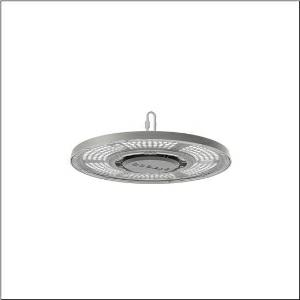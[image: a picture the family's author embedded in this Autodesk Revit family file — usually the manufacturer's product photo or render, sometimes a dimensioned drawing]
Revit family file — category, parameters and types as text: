
# Revit family: highbay_31-l_51hc41da4jmb
name_source: partatom
category: Lighting Fixtures
units: mm (PartAtom-declared; Revit-internal decimal feet)

## family parameters
Cut with Voids When Loaded = No
Host = Face
Light Source = No
Part Type = Normal
Room Calculation Point = No
Round Connector Dimension = Use Diameter
Shared = No

## types (1)
- Highbay 31-L (1 x LED, 20000 lm, 134 W, 4000K)
    Apparent Load = 134 VA
    CIE Flux Codes = 95 98 100 100 100
    Color Rendering = 80
    Color Temperature = 4000K
    Default Elevation = 1800 mm
    Description = Highbay 31-L, LED high bay luminaire, primary light control with lens, of PC, primary optical cover: cover panel, of PC, transparent, light emission: direct distribution, primary light characteristic: rotationally symmetric, installation type: suspended mounting, surface-mounted, LED, rated luminous flux: 20.000lm, luminous efficacy: 150lm/W, light colour: 840, colour temperature: 4000K, control gear: ECG DALI, with cable, 5x 1.0mm², free wire ends, mains connection: 220..240V, AC/DC, 0/50..60Hz, cable length: 1,5m, rated input power: 134W, housing, rotationally symmetric, of diecast aluminium, grey aluminium (RAL 9007), diameter: 404mm, protection rating (complete): IP65, insulation class (complete): insulation class I (protective earthing), certification: CE, ENEC, UKCA, protection symbol: D, impact resistance: IK08, permissible operating ambient temperature: -30..+45°C, standard: EN 60598-2-22, EN 60598, corresponds to IFS (International Featured Standards) requirements for safety and quality in the food industry, packaging unit: 1 piece
    Height = 141 mm
    Lamp = 1 x LED
    Lamp Light Flux = 20000 lm
    Lamp Power = 134 W
    Lamp count = 1
    Length = 406 mm
    Luminous efficacy = 149 lm/W
    Manufacturer = Siteco
    ModVariant = No
    Model = 51HC41DA4JMB
    Mounting Place = Ceiling
    Mounting Type = Pendant
    Number of Poles = 1
    OnlyDefault = Yes
    Power Factor = 1
    Product Name = Highbay 31-L
    Product group = LED high bay luminaire
    ProductGroupID = 903
    Protection Class = Protection class I
    Protection Degree = IP 65
    RLX_Detail_Level = 1
    RlxData = <blob elided: 108489 chars, md5=3aebd5d9>
    Socket = socket
    Standby Power = 0 W
    System Light Flux = 20000 lm
    System Power = 134 W
    Type Comments = Product without accessories
    Type Image = l_1007237.jpg
    URL = http://relux.com
    VarID = ---
    Voltage = 0 V
    Weight = 0.00 kg
    Width = 0 mm  [stored 0 ft]

note: [stored X ft] marks values corroborated as IEEE doubles in the binary element streams (Revit-internal decimal feet)

## geometry (parser evidence)
native form markers: Blend x4, Sweep x9
no freeform markers — native parametric forms only
